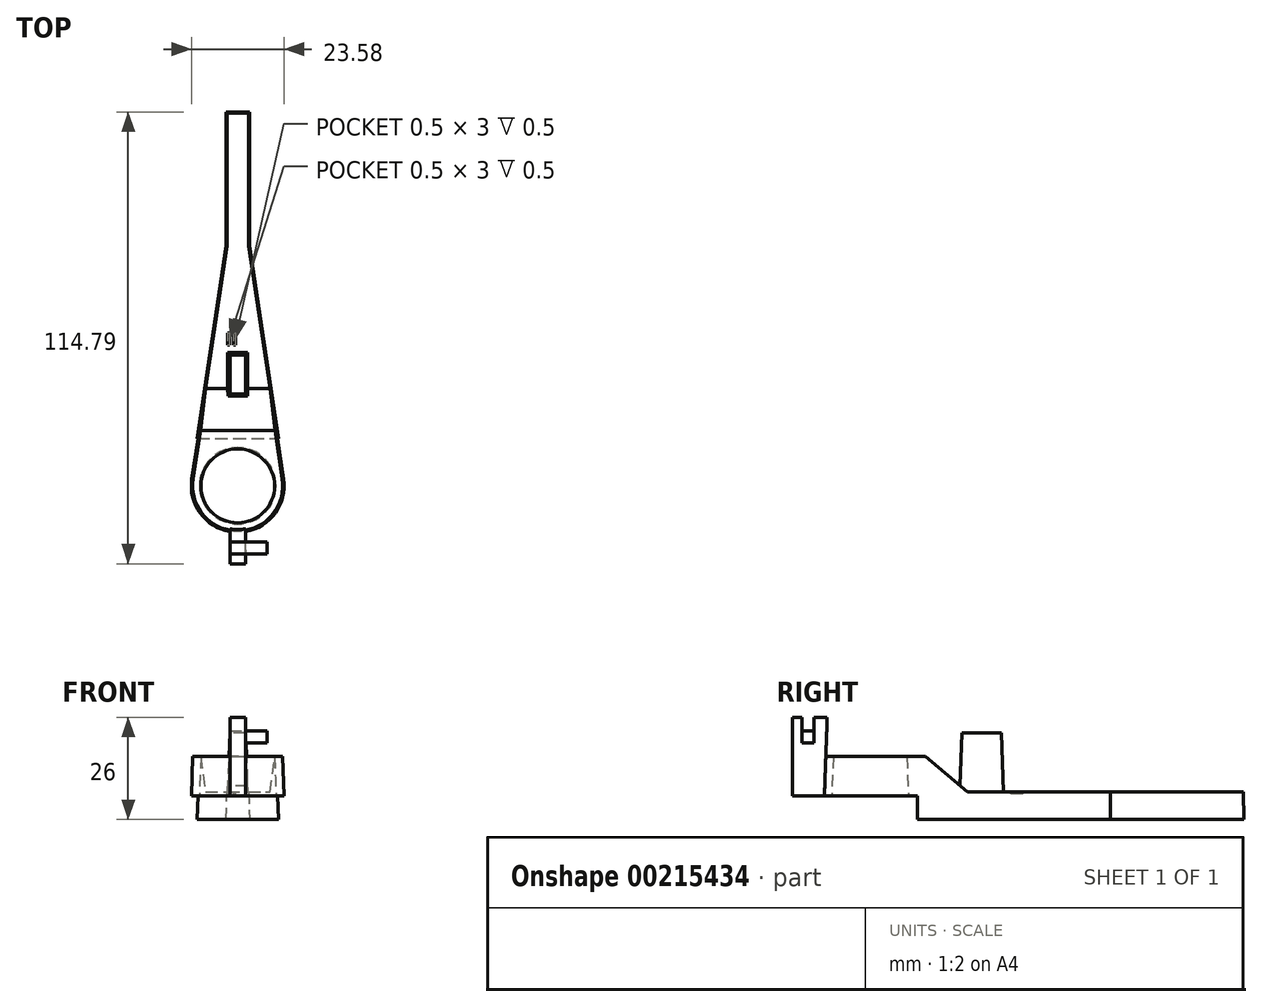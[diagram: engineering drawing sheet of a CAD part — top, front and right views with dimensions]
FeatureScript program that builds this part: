
annotation { "Feature Type Name" : "Feature", "Feature Type Description" : "" }
export const myFeature = defineFeature(function(context is Context, id is Id, definition is map)
    precondition{}
    {
        {
            var Q0;
            Q0=qCreatedBy(makeId("Top.planeOp"),FACE);
            var sketch = newSketch(context, id + "F0", { "sketchPlane" : qUnion([Q0])});
            skCircle(sketch, "E0", {"center": v(0, 0) * mm, "radius": 12 * mm});
            skLineSegment(sketch, "E1", {"start": v(-3, 95) * mm, "end": v(3, 95) * mm});
            skLineSegment(sketch, "E2", {"start": v(0, -12) * mm, "end": v(0, 95) * mm, "construction": true});
            skPoint(sketch, "E3", {"position": v(0, 95) * mm});
            skLineSegment(sketch, "E4", {"start": v(-3, 95) * mm, "end": v(-3, 61) * mm});
            skLineSegment(sketch, "E5", {"start": v(3, 95) * mm, "end": v(3, 61) * mm});
            skLineSegment(sketch, "E6", {"start": v(-3, 61) * mm, "end": v(-11.87, 1.78) * mm});
            skLineSegment(sketch, "E7", {"start": v(3, 61) * mm, "end": v(11.87, 1.78) * mm});
            skSolve(sketch);
        }
        {
            var Q0;
            Q0=qSketchRegion(id+"F0",true);
            extrude(context, id + "F1", {"entities" : qUnion([Q0]), "depth" : 16 * mm, "hasDraft" : true, "draftAngle" : 2 * degree, "draftPullDirection" : true});
        }
        {
            var Q0;
            Q0=qCreatedBy(makeId("Right.planeOp"),FACE);
            cPlane(context, id + "F2", {"entities" : qUnion([Q0]), "cplaneType" : CPlaneType.OFFSET, "offset" : 12 * mm, "width" : 150 * mm, "height" : 150 * mm});
        }
        {
            var Q0;
            Q0=qCreatedBy(id+"F2.planeOp",FACE);
            var sketch = newSketch(context, id + "F3", { "sketchPlane" : qUnion([Q0])});
            skLineSegment(sketch, "E8", {"start": v(94.76, 7) * mm, "end": v(24.76, 7) * mm});
            skLineSegment(sketch, "E9", {"start": v(24.76, 7) * mm, "end": v(14.03, 16) * mm});
            skLineSegment(sketch, "E10", {"start": v(12, 0) * mm, "end": v(12, 6) * mm});
            skLineSegment(sketch, "E11", {"start": v(12, 6) * mm, "end": v(-11.8, 6) * mm});
            skLineSegment(sketch, "E12", {"start": v(12, 0) * mm, "end": v(-12, 0) * mm});
            skLineSegment(sketch, "E13", {"start": v(-12, 0) * mm, "end": v(-11.8, 6) * mm});
            skLineSegment(sketch, "E14", {"start": v(14.03, 16) * mm, "end": v(94.44, 16) * mm});
            skLineSegment(sketch, "E15", {"start": v(94.44, 16) * mm, "end": v(94.76, 7) * mm});
            skSolve(sketch);
        }
        {
            var Q0;
            Q0=qSketchRegion(id+"F3",true);
            extrude(context, id + "F4", {"entities" : qUnion([Q0]), "operationType" : NewBodyOperationType.REMOVE, "endBound" : BoundingType.THROUGH_ALL, "oppositeDirection" : true, "depth" : 25 * mm});
        }
        {
            var Q0;
            Q0=makeQuery(id+"F4.boolean.opBoolean","COPY",FACE,{"derivedFrom":makeQuery(id+"F4.opExtrude","SWEPT_FACE",FACE,{"disambiguationData":[OSD([sQuery(id+"F3.wireOp",EDGE,"E8")])]})});
            cPlane(context, id + "F5", {"entities" : qUnion([Q0]), "cplaneType" : CPlaneType.OFFSET, "offset" : 15 * mm, "width" : 150 * mm, "height" : 150 * mm});
        }
        {
            var Q0;
            Q0=qCreatedBy(id+"F5.planeOp",FACE);
            var sketch = newSketch(context, id + "F6", { "sketchPlane" : qUnion([Q0])});
            skLineSegment(sketch, "E16.bottom", {"start": v(-2, 23.3) * mm, "end": v(2, 23.3) * mm});
            skLineSegment(sketch, "E16.top", {"start": v(-2, 33.3) * mm, "end": v(2, 33.3) * mm});
            skLineSegment(sketch, "E16.left", {"start": v(-2, 23.3) * mm, "end": v(-2, 33.3) * mm});
            skLineSegment(sketch, "E16.right", {"start": v(2, 23.3) * mm, "end": v(2, 33.3) * mm});
            skPoint(sketch, "E16.middle", {"position": v(0, 28.3) * mm});
            skSolve(sketch);
        }
        {
            var Q0;
            Q0=qSketchRegion(id+"F6",true);
            extrude(context, id + "F7", {"entities" : qUnion([Q0]), "operationType" : NewBodyOperationType.ADD, "endBound" : BoundingType.UP_TO_NEXT, "oppositeDirection" : true, "depth" : 25 * mm, "hasDraft" : true, "draftAngle" : 2 * degree});
        }
        {
            var Q0;
            Q0=makeQuery(id+"F4.boolean.opBoolean","COPY",FACE,{"derivedFrom":makeQuery(id+"F4.opExtrude","SWEPT_FACE",FACE,{"disambiguationData":[OSD([sQuery(id+"F3.wireOp",EDGE,"E11")])]})});
            var sketch = newSketch(context, id + "F8", { "sketchPlane" : qUnion([Q0])});
            skCircle(sketch, "E17", {"center": v(0, 0) * mm, "radius": 9.72 * mm});
            skSolve(sketch);
        }
        {
            var Q0;
            Q0=qSketchRegion(id+"F8",true);
            extrude(context, id + "F9", {"entities" : qUnion([Q0]), "operationType" : NewBodyOperationType.REMOVE, "endBound" : BoundingType.THROUGH_ALL, "oppositeDirection" : true, "depth" : 25 * mm, "hasDraft" : true, "draftAngle" : 2 * degree, "draftPullDirection" : true});
        }
        {
            var Q0;
            Q0=makeQuery(id+"F4.boolean.opBoolean","COPY",FACE,{"derivedFrom":makeQuery(id+"F4.opExtrude","SWEPT_FACE",FACE,{"disambiguationData":[OSD([sQuery(id+"F3.wireOp",EDGE,"E11")])]})});
            var sketch = newSketch(context, id + "F10", { "sketchPlane" : qUnion([Q0])});
            skLineSegment(sketch, "E18", {"start": v(0, 11.8) * mm, "end": v(0, 19.8) * mm, "construction": true});
            skPoint(sketch, "E18.endSnap0", {"position": v(0, 11.8) * mm});
            skLineSegment(sketch, "E19", {"start": v(0, 19.8) * mm, "end": v(-2, 19.8) * mm});
            skLineSegment(sketch, "E20", {"start": v(-2, 19.8) * mm, "end": v(-2, 11.62) * mm});
            skLineSegment(sketch, "E21", {"start": v(0, 19.8) * mm, "end": v(2, 19.8) * mm});
            skLineSegment(sketch, "E22", {"start": v(2, 19.8) * mm, "end": v(2, 11.62) * mm});
            skArc(sketch, "E23", {"start": v(2, 11.62) * mm, "mid": v(0, 11.8) * mm, "end": v(-2, 11.62) * mm});
            skSolve(sketch);
        }
        {
            var Q0;
            Q0=qCreatedBy(makeId("Front.planeOp"),FACE);
            var Q1;
            Q1=sQuery(id+"F10.wireOp",VERTEX,"E21.start");
            cPlane(context, id + "F11", {"entities" : qUnion([Q0, Q1]), "cplaneType" : CPlaneType.PLANE_POINT, "offset" : 25 * mm, "width" : 150 * mm, "height" : 150 * mm});
        }
        {
            var Q0;
            Q0=qCreatedBy(id+"F11.planeOp",FACE);
            var sketch = newSketch(context, id + "F12", { "sketchPlane" : qUnion([Q0])});
            skLineSegment(sketch, "E24.bottom", {"start": v(-2, 6) * mm, "end": v(2, 6) * mm});
            skLineSegment(sketch, "E24.top", {"start": v(-2, 26) * mm, "end": v(2, 26) * mm});
            skLineSegment(sketch, "E24.left", {"start": v(-2, 6) * mm, "end": v(-2, 26) * mm});
            skLineSegment(sketch, "E24.right", {"start": v(2, 6) * mm, "end": v(2, 26) * mm});
            skSolve(sketch);
        }
        {
            var Q0;
            Q0=qSketchRegion(id+"F12",true);
            var Q1;
            Q1=makeQuery(id+"F1.opExtrude","SWEPT_FACE",FACE,{"disambiguationData":[OSD([sQuery(id+"F0.wireOp",EDGE,"E0")])]});
            extrude(context, id + "F13", {"entities" : qUnion([Q0]), "operationType" : NewBodyOperationType.ADD, "endBound" : BoundingType.UP_TO_SURFACE, "oppositeDirection" : true, "endBoundEntityFace" : qUnion([Q1]), "depth" : 8 * mm});
        }
        {
            var Q0;
            Q0=makeQuery(id+"F13.opExtrude","SWEPT_FACE",FACE,{"disambiguationData":[OSD([sQuery(id+"F12.wireOp",EDGE,"E24.right")])]});
            var sketch = newSketch(context, id + "F14", { "sketchPlane" : qUnion([Q0])});
            skLineSegment(sketch, "E25.bottom", {"start": v(-17.3, 22.5) * mm, "end": v(-14.3, 22.5) * mm});
            skLineSegment(sketch, "E25.top", {"start": v(-17.3, 19.5) * mm, "end": v(-14.3, 19.5) * mm});
            skLineSegment(sketch, "E25.left", {"start": v(-17.3, 22.5) * mm, "end": v(-17.3, 19.5) * mm});
            skLineSegment(sketch, "E25.right", {"start": v(-14.3, 22.5) * mm, "end": v(-14.3, 19.5) * mm});
            skSolve(sketch);
        }
        {
            var Q0;
            Q0=qSketchRegion(id+"F14",true);
            extrude(context, id + "F15", {"entities" : qUnion([Q0]), "operationType" : NewBodyOperationType.ADD, "depth" : 5.5 * mm});
        }
        {
            var Q0;
            Q0=makeQuery(id+"F13.opExtrude","SWEPT_FACE",FACE,{"disambiguationData":[OSD([sQuery(id+"F12.wireOp",EDGE,"E24.right")])]});
            var sketch = newSketch(context, id + "F16", { "sketchPlane" : qUnion([Q0])});
            skLineSegment(sketch, "E26.bottom", {"start": v(-17.3, 22.5) * mm, "end": v(-14.3, 22.5) * mm});
            skLineSegment(sketch, "E26.top", {"start": v(-17.3, 26) * mm, "end": v(-14.3, 26) * mm});
            skLineSegment(sketch, "E26.left", {"start": v(-17.3, 22.5) * mm, "end": v(-17.3, 26) * mm});
            skLineSegment(sketch, "E26.right", {"start": v(-14.3, 22.5) * mm, "end": v(-14.3, 26) * mm});
            skSolve(sketch);
        }
        {
            var Q0;
            Q0=qSketchRegion(id+"F16",true);
            extrude(context, id + "F17", {"entities" : qUnion([Q0]), "operationType" : NewBodyOperationType.REMOVE, "endBound" : BoundingType.THROUGH_ALL, "oppositeDirection" : true, "depth" : 25 * mm});
        }
        {
            var Q0;
            Q0=makeQuery(id+"F4.boolean.opBoolean","COPY",FACE,{"derivedFrom":makeQuery(id+"F4.opExtrude","SWEPT_FACE",FACE,{"disambiguationData":[OSD([sQuery(id+"F3.wireOp",EDGE,"E8")])]})});
            var sketch = newSketch(context, id + "F18", { "sketchPlane" : qUnion([Q0])});
            skLineSegment(sketch, "E27.bottom", {"start": v(-2.52, 38.82) * mm, "end": v(-2.02, 38.82) * mm});
            skLineSegment(sketch, "E27.top", {"start": v(-2.52, 35.82) * mm, "end": v(-2.02, 35.82) * mm});
            skLineSegment(sketch, "E27.left", {"start": v(-2.52, 38.82) * mm, "end": v(-2.52, 35.82) * mm});
            skLineSegment(sketch, "E27.right", {"start": v(-2.02, 38.82) * mm, "end": v(-2.02, 35.82) * mm});
            skLineSegment(sketch, "E28.bottom", {"start": v(-1.02, 38.82) * mm, "end": v(-0.52, 38.82) * mm});
            skLineSegment(sketch, "E28.top", {"start": v(-1.02, 35.82) * mm, "end": v(-0.52, 35.82) * mm});
            skLineSegment(sketch, "E28.left", {"start": v(-0.52, 38.82) * mm, "end": v(-0.52, 35.82) * mm});
            skLineSegment(sketch, "E28.right", {"start": v(-1.02, 38.82) * mm, "end": v(-1.02, 35.82) * mm});
            skSolve(sketch);
        }
        {
            var Q0;
            Q0 = qSketchRegion(id + "F18", true);
            extrude(context, id + "F19", {"entities" : qUnion([Q0]), "operationType" : NewBodyOperationType.REMOVE, "oppositeDirection" : true, "depth" : 0.5 * mm});
        }
    });
